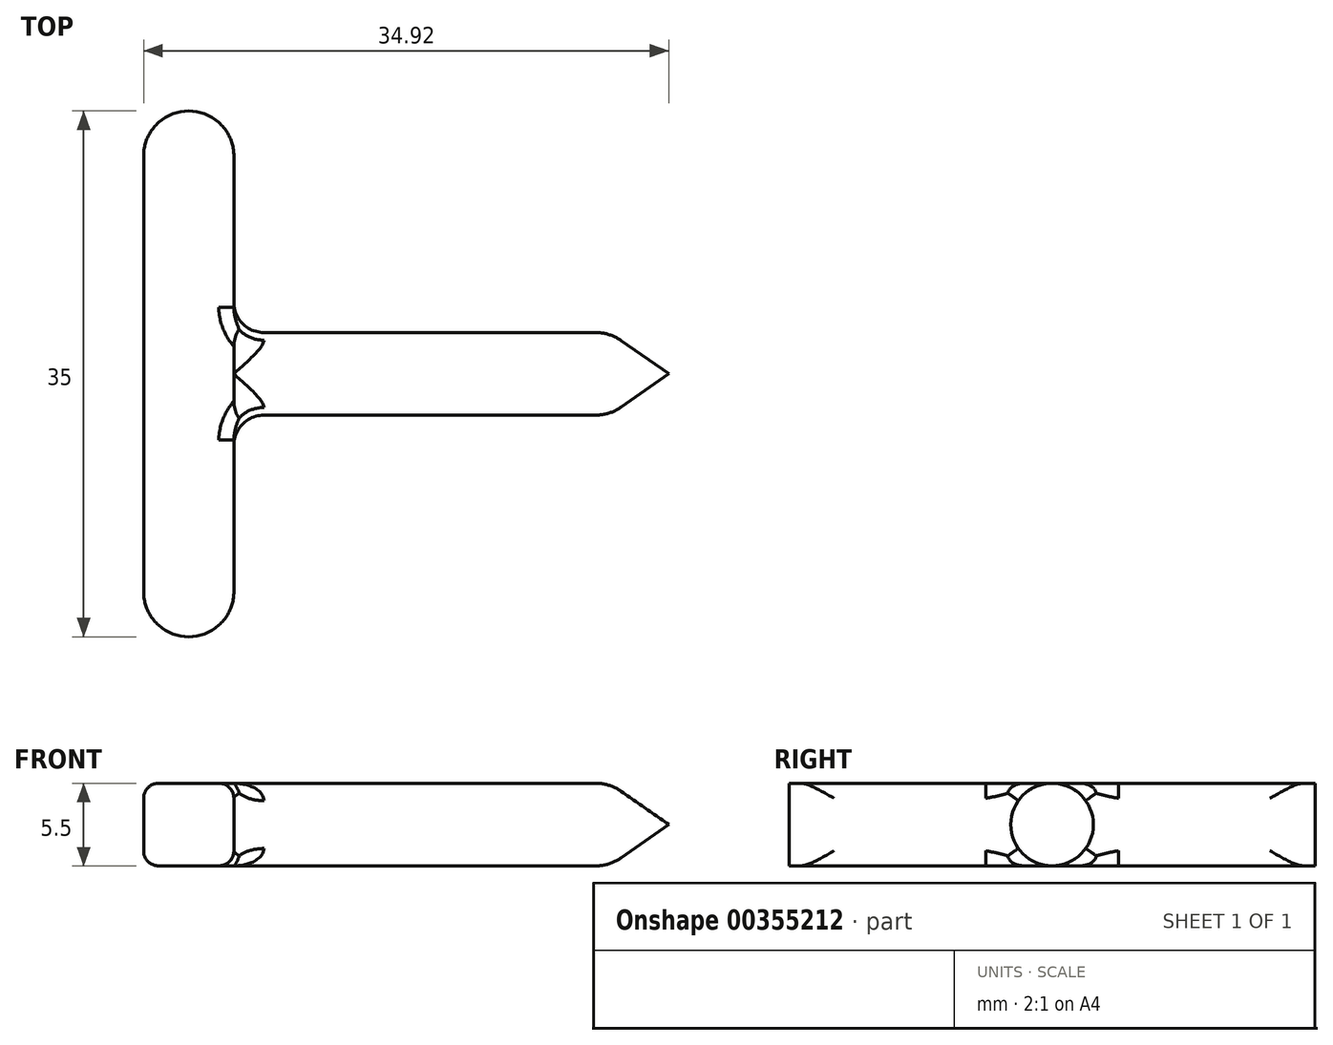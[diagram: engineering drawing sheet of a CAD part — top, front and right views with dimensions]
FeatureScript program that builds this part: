
annotation { "Feature Type Name" : "Feature", "Feature Type Description" : "" }
export const myFeature = defineFeature(function(context is Context, id is Id, definition is map)
    precondition{}
    {
        {
            var Q0;
            Q0=qCreatedBy(makeId("Top.planeOp"),FACE);
            var sketch = newSketch(context, id + "F0", { "sketchPlane" : qUnion([Q0])});
            skLineSegment(sketch, "E0", {"start": v(-14.46, 2.75) * mm, "end": v(10.54, 2.75) * mm});
            skLineSegment(sketch, "E1", {"start": v(10.54, 2.75) * mm, "end": v(14.46, 0) * mm});
            skLineSegment(sketch, "E2", {"start": v(-14.46, 0) * mm, "end": v(14.46, 0) * mm});
            skLineSegment(sketch, "E3", {"start": v(-14.46, 2.75) * mm, "end": v(-14.46, 0) * mm});
            skSolve(sketch);
        }
        {
            var Q0;
            Q0=makeQuery(id+"F0.imprint","IMPRINT",FACE,{"disambiguationData":[TD([[makeQuery(id+"F0.imprint","IMPRINT",EDGE,{"derivedFrom":sQuery(id+"F0.wireOp",EDGE,"E0")}),-1.0]])]});
            var Q1;
            Q1=sQuery(id+"F0.wireOp",EDGE,"E2");
            revolve(context, id + "F1", {"entities" : qUnion([Q0]), "axis" : qUnion([Q1]), "revolveType" : RevolveType.FULL});
        }
        {
            var Q0;
            Q0=makeQuery(id+"F1.opRevolve","SWEPT_EDGE",EDGE,{"disambiguationData":[OSD([sQuery(id+"F0.wireOp",EDGE,"E0"),sQuery(id+"F0.wireOp",EDGE,"E1")])]});
            fillet(context, id + "F2", {"entities" : qUnion([Q0]), "radius" : 3 * mm, "allowEdgeOverflow" : false});
        }
        {
            var Q0;
            Q0=makeQuery(id+"F1.opRevolve","SWEPT_FACE",FACE,{"disambiguationData":[OSD([sQuery(id+"F0.wireOp",EDGE,"E3")])]});
            var sketch = newSketch(context, id + "F3", { "sketchPlane" : qUnion([Q0])});
            skLineSegment(sketch, "E4.bottom", {"start": v(17.5, 2.75) * mm, "end": v(-17.5, 2.75) * mm});
            skLineSegment(sketch, "E4.top", {"start": v(17.5, -2.75) * mm, "end": v(-17.5, -2.75) * mm});
            skLineSegment(sketch, "E4.left", {"start": v(17.5, 2.75) * mm, "end": v(17.5, -2.75) * mm});
            skLineSegment(sketch, "E4.right", {"start": v(-17.5, 2.75) * mm, "end": v(-17.5, -2.75) * mm});
            skPoint(sketch, "E4.middle", {"position": v(0, 0) * mm});
            skSolve(sketch);
        }
        {
            var Q0;
            {var subQ0=sQuery(id+"F3.wireOp",EDGE,"E4.right");Q0=makeQuery(id+"F3.imprint","IMPRINT",FACE,{"disambiguationData":[TD([[makeQuery(id+"F3.imprint","IMPRINT",EDGE,{"derivedFrom":subQ0}),1.0]])]});}
            var Q1;
            {var subQ0=sQuery(id+"F3.wireOp",EDGE,"E4.left");Q1=makeQuery(id+"F3.imprint","IMPRINT",FACE,{"disambiguationData":[TD([[makeQuery(id+"F3.imprint","IMPRINT",EDGE,{"derivedFrom":subQ0}),-1.0]])]});}
            var Q2;
            {var subQ0=makeQuery(id+"F1.opRevolve","SWEPT_EDGE",EDGE,{"disambiguationData":[OSD([sQuery(id+"F0.wireOp",EDGE,"E0"),sQuery(id+"F0.wireOp",EDGE,"E3")])]});var subQ1=makeQuery(id+"F3.imprint","INTERSECT",VERTEX,{"derivedFrom":[subQ0,sQuery(id+"F3.wireOp",EDGE,"E4.bottom")]});Q2=makeQuery(id+"F3.imprint","IMPRINT",FACE,{"disambiguationData":[TD([[makeQuery(id+"F3.imprint","IMPRINT",EDGE,{"disambiguationData":[TD([[subQ1,1.0]])],"derivedFrom":subQ0}),1.0]])]});}
            extrude(context, id + "F4", {"entities" : qUnion([Q0, Q1, Q2]), "operationType" : NewBodyOperationType.ADD, "depth" : 6 * mm});
        }
        {
            var Q0;
            Q0=makeQuery(id+"F4.opExtrude","CAP_EDGE",EDGE,{"disambiguationData":[OSD([sQuery(id+"F3.wireOp",EDGE,"E4.right")])],"isStart":false});
            var Q1;
            Q1=makeQuery(id+"F4.opExtrude","CAP_EDGE",EDGE,{"disambiguationData":[OSD([sQuery(id+"F3.wireOp",EDGE,"E4.right")])],"isStart":true});
            var Q2;
            Q2=makeQuery(id+"F4.opExtrude","CAP_EDGE",EDGE,{"disambiguationData":[OSD([sQuery(id+"F3.wireOp",EDGE,"E4.left")])],"isStart":false});
            var Q3;
            Q3=makeQuery(id+"F4.opExtrude","CAP_EDGE",EDGE,{"disambiguationData":[OSD([sQuery(id+"F3.wireOp",EDGE,"E4.left")])],"isStart":true});
            fillet(context, id + "F5", {"entities" : qUnion([Q0, Q1, Q2, Q3]), "radius" : 3 * mm, "tangentPropagation" : true, "allowEdgeOverflow" : false});
        }
        {
            var Q0;
            Q0=makeQuery(id+"F4.boolean.opBoolean","SPLIT",EDGE,{"disambiguationData":[OD(1.0)],"derivedFrom":makeQuery(id+"F1.opRevolve","SWEPT_EDGE",EDGE,{"disambiguationData":[OSD([sQuery(id+"F0.wireOp",EDGE,"E0"),sQuery(id+"F0.wireOp",EDGE,"E3")])]})});
            var Q1;
            Q1=makeQuery(id+"F4.boolean.opBoolean","SPLIT",EDGE,{"disambiguationData":[OD(0.0)],"derivedFrom":makeQuery(id+"F1.opRevolve","SWEPT_EDGE",EDGE,{"disambiguationData":[OSD([sQuery(id+"F0.wireOp",EDGE,"E0"),sQuery(id+"F0.wireOp",EDGE,"E3")])]})});
            fillet(context, id + "F6", {"entities" : qUnion([Q0, Q1]), "radius" : 2 * mm, "tangentPropagation" : true, "allowEdgeOverflow" : false});
        }
        {
            var Q0;
            Q0=makeQuery(id+"F4.opExtrude","CAP_EDGE",EDGE,{"disambiguationData":[OSD([sQuery(id+"F3.wireOp",EDGE,"E4.bottom")])],"isStart":false});
            var Q1;
            Q1=makeQuery(id+"F4.opExtrude","CAP_EDGE",EDGE,{"disambiguationData":[OSD([sQuery(id+"F3.wireOp",EDGE,"E4.top")])],"isStart":false});
            var Q2;
            Q2=makeQuery(id+"F5.opFillet","BLEND_EDGE",EDGE,{"blendedFrom":[makeQuery(id+"F4.opExtrude","CAP_EDGE",EDGE,{"disambiguationData":[OSD([sQuery(id+"F3.wireOp",EDGE,"E4.right")])],"isStart":false}),makeQuery(id+"F4.opExtrude","SWEPT_FACE",FACE,{"disambiguationData":[OSD([sQuery(id+"F3.wireOp",EDGE,"E4.bottom")])]})],"blendedInto":[makeQuery(id+"F4.opExtrude","SWEPT_FACE",FACE,{"disambiguationData":[OSD([sQuery(id+"F3.wireOp",EDGE,"E4.bottom")])]})]});
            var Q3;
            {var subQ0=sQuery(id+"F3.wireOp",EDGE,"E4.right");var subQ1=sQuery(id+"F3.wireOp",EDGE,"E4.bottom");Q3=makeQuery(id+"F4.boolean.opBoolean","SPLIT",EDGE,{"disambiguationData":[TD([makeQuery(id+"F4.opExtrude","SWEPT_FACE",FACE,{"disambiguationData":[OSD([subQ0])]})])],"derivedFrom":makeQuery(id+"F4.opExtrude","CAP_EDGE",EDGE,{"disambiguationData":[OSD([subQ1])],"isStart":true})});}
            var Q4;
            {var subQ0=sQuery(id+"F3.wireOp",EDGE,"E4.left");var subQ1=sQuery(id+"F3.wireOp",EDGE,"E4.bottom");Q4=makeQuery(id+"F4.boolean.opBoolean","SPLIT",EDGE,{"disambiguationData":[TD([makeQuery(id+"F4.opExtrude","SWEPT_FACE",FACE,{"disambiguationData":[OSD([subQ0])]})])],"derivedFrom":makeQuery(id+"F4.opExtrude","CAP_EDGE",EDGE,{"disambiguationData":[OSD([subQ1])],"isStart":true})});}
            var Q5;
            Q5=makeQuery(id+"F5.opFillet","BLEND_EDGE",EDGE,{"blendedFrom":[makeQuery(id+"F4.opExtrude","CAP_EDGE",EDGE,{"disambiguationData":[OSD([sQuery(id+"F3.wireOp",EDGE,"E4.left")])],"isStart":false}),makeQuery(id+"F4.opExtrude","SWEPT_FACE",FACE,{"disambiguationData":[OSD([sQuery(id+"F3.wireOp",EDGE,"E4.bottom")])]})],"blendedInto":[makeQuery(id+"F4.opExtrude","SWEPT_FACE",FACE,{"disambiguationData":[OSD([sQuery(id+"F3.wireOp",EDGE,"E4.bottom")])]})]});
            var Q6;
            Q6=makeQuery(id+"F5.opFillet","BLEND_EDGE",EDGE,{"blendedFrom":[makeQuery(id+"F4.opExtrude","CAP_EDGE",EDGE,{"disambiguationData":[OSD([sQuery(id+"F3.wireOp",EDGE,"E4.right")])],"isStart":false}),makeQuery(id+"F4.opExtrude","SWEPT_FACE",FACE,{"disambiguationData":[OSD([sQuery(id+"F3.wireOp",EDGE,"E4.top")])]})],"blendedInto":[makeQuery(id+"F4.opExtrude","SWEPT_FACE",FACE,{"disambiguationData":[OSD([sQuery(id+"F3.wireOp",EDGE,"E4.top")])]})]});
            var Q7;
            Q7=makeQuery(id+"F5.opFillet","BLEND_EDGE",EDGE,{"blendedFrom":[makeQuery(id+"F4.opExtrude","CAP_EDGE",EDGE,{"disambiguationData":[OSD([sQuery(id+"F3.wireOp",EDGE,"E4.left")])],"isStart":false}),makeQuery(id+"F4.opExtrude","SWEPT_FACE",FACE,{"disambiguationData":[OSD([sQuery(id+"F3.wireOp",EDGE,"E4.top")])]})],"blendedInto":[makeQuery(id+"F4.opExtrude","SWEPT_FACE",FACE,{"disambiguationData":[OSD([sQuery(id+"F3.wireOp",EDGE,"E4.top")])]})]});
            var Q8;
            {var subQ0=sQuery(id+"F3.wireOp",EDGE,"E4.left");var subQ1=sQuery(id+"F3.wireOp",EDGE,"E4.top");Q8=makeQuery(id+"F4.boolean.opBoolean","SPLIT",EDGE,{"disambiguationData":[TD([makeQuery(id+"F4.opExtrude","SWEPT_FACE",FACE,{"disambiguationData":[OSD([subQ0])]})])],"derivedFrom":makeQuery(id+"F4.opExtrude","CAP_EDGE",EDGE,{"disambiguationData":[OSD([subQ1])],"isStart":true})});}
            var Q9;
            {var subQ0=sQuery(id+"F3.wireOp",EDGE,"E4.right");var subQ1=sQuery(id+"F3.wireOp",EDGE,"E4.top");Q9=makeQuery(id+"F4.boolean.opBoolean","SPLIT",EDGE,{"disambiguationData":[TD([makeQuery(id+"F4.opExtrude","SWEPT_FACE",FACE,{"disambiguationData":[OSD([subQ0])]})])],"derivedFrom":makeQuery(id+"F4.opExtrude","CAP_EDGE",EDGE,{"disambiguationData":[OSD([subQ1])],"isStart":true})});}
            fillet(context, id + "F7", {"entities" : qUnion([Q0, Q1, Q2, Q3, Q4, Q5, Q6, Q7, Q8, Q9]), "radius" : 1 * mm, "allowEdgeOverflow" : false});
        }
    });
